# Revit family: FP-Revit20-en-CG151DNGGB5-GasCooktop-0-90004039A-US-CA
name_source: partatom
category: Generic Models
units: mm (PartAtom-declared; Revit-internal decimal feet)

## family parameters
Always vertical = No
Can host rebar = No
Cut with Voids When Loaded = No
Part Type = Normal
Room Calculation Point = No
Round Connector Dimension = Use Diameter
Shared = No
Work Plane-Based = Yes

## types (1)
- CG151DNGGB5 (Black)
    Chassis - Depth = 485 mm  [stored 1.59121 ft]
    Chassis - Height = 61 mm  [stored 0.200131 ft]
    Chassis - Width = 345 mm  [stored 1.13189 ft]
    Clearance - Combustible = Fisher & Paykel - Clearance Required (Combustible)
    Clearance - Non-Combustible = Fisher & Paykel - Clearance Required (Non-Combustible)
    Clearance - Overhead Combustible = 650 mm  [stored 2.13255 ft]
    Clearance - Overhead Exhaust Fan = 800 mm  [stored 2.62467 ft]
    Clearance - Overhead Non-Combustible = 500 mm  [stored 1.64042 ft]
    Clearance - Overhead Rangehood = Fisher & Paykel - Clearance Required (Rangehood)
    Clearance - Rear Combustible = 85 mm  [stored 0.278871 ft]
    Clearance - Side Combustible = 120 mm  [stored 0.393701 ft]
    Cooktop Glass = Fisher & Paykel - Glass, Black
    Default Elevation = 1219 mm
    Description = Gas on Glass Modular Cooktop, 15"
    Manufacturer = Fisher & Paykel Appliances
    Model = CG151DNGGB5
    Product - Depth = 530 mm  [stored 1.73885 ft]
    Product - Height = 127 mm  [stored 0.416667 ft]
    Product - Width = 385 mm  [stored 1.26312 ft]
    URL = www.fisherpaykel.com

note: [stored X ft] marks values corroborated as IEEE doubles in the binary element streams (Revit-internal decimal feet)

## geometry (parser evidence)
native form markers: Sweep x11
no freeform markers — native parametric forms only
